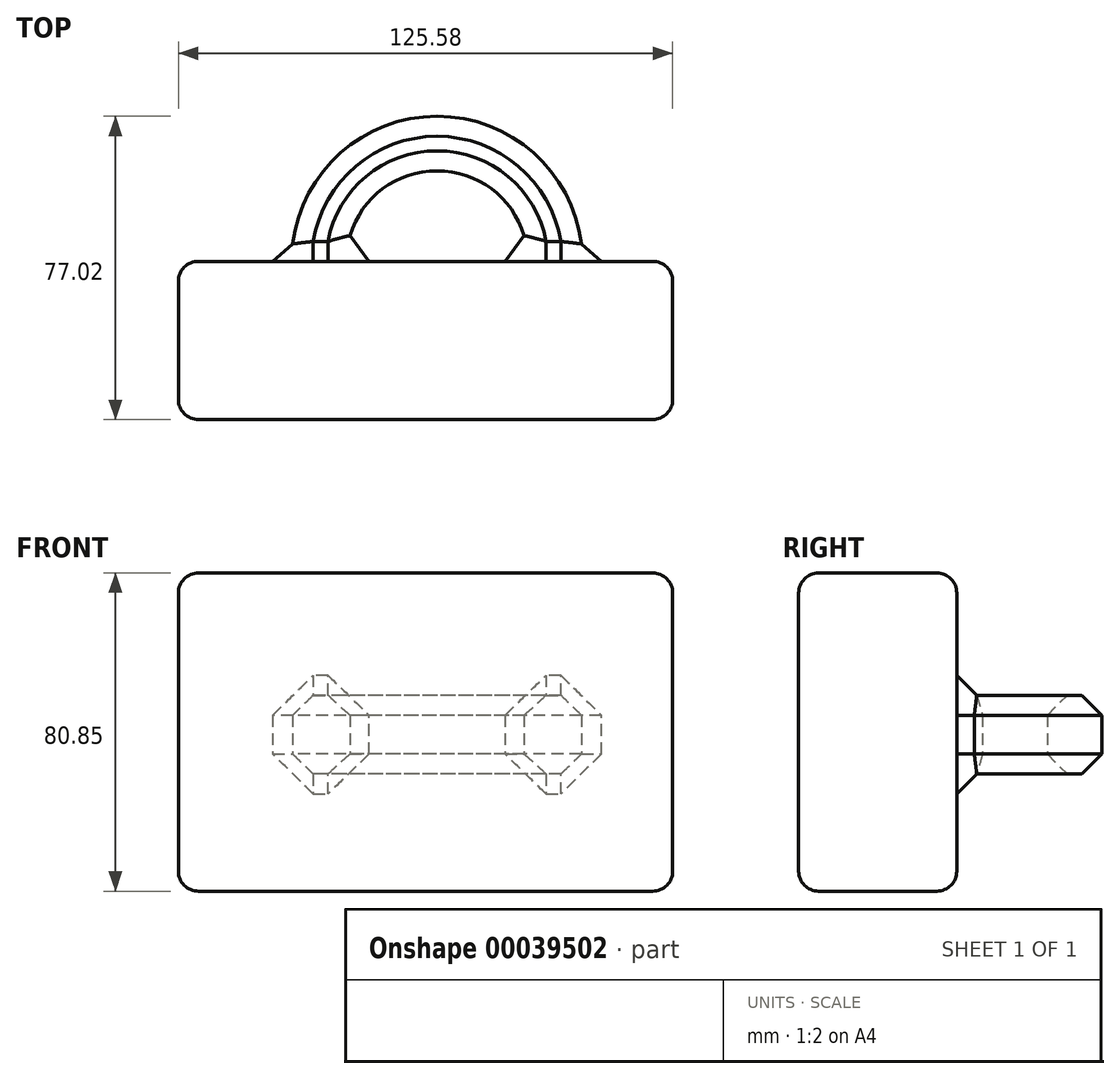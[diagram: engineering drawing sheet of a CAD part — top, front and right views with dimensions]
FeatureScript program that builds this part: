
annotation { "Feature Type Name" : "Feature", "Feature Type Description" : "" }
export const myFeature = defineFeature(function(context is Context, id is Id, definition is map)
    precondition{}
    {
        {
            var Q0;
            Q0=qCreatedBy(makeId("Top.planeOp"),FACE);
            var sketch = newSketch(context, id + "F0", { "sketchPlane" : qUnion([Q0])});
            skCircle(sketch, "E0", {"center": v(0.24, -0.12) * mm, "radius": 36.97 * mm});
            skCircle(sketch, "E1", {"center": v(0.24, -0.12) * mm, "radius": 23.11 * mm});
            skSolve(sketch);
        }
        {
            var Q0;
            Q0=makeQuery(id+"F0.imprint","IMPRINT",FACE,{"disambiguationData":[TD([[makeQuery(id+"F0.imprint","IMPRINT",EDGE,{"derivedFrom":sQuery(id+"F0.wireOp",EDGE,"E0")}),1.0]])]});
            extrude(context, id + "F1", {"entities" : qUnion([Q0]), "depth" : 20 * mm});
        }
        {
            var Q0;
            Q0=qCreatedBy(makeId("Front.planeOp"),FACE);
            var sketch = newSketch(context, id + "F2", { "sketchPlane" : qUnion([Q0])});
            skLineSegment(sketch, "E2.bottom", {"start": v(60.11, 51.07) * mm, "end": v(-65.47, 51.07) * mm});
            skLineSegment(sketch, "E2.top", {"start": v(60.11, -29.78) * mm, "end": v(-65.47, -29.78) * mm});
            skLineSegment(sketch, "E2.left", {"start": v(60.11, 51.07) * mm, "end": v(60.11, -29.78) * mm});
            skLineSegment(sketch, "E2.right", {"start": v(-65.47, 51.07) * mm, "end": v(-65.47, -29.78) * mm});
            skSolve(sketch);
        }
        {
            var Q0;
            Q0=makeQuery(id+"F2.imprint","IMPRINT",FACE,{"disambiguationData":[TD([[makeQuery(id+"F2.imprint","IMPRINT",EDGE,{"derivedFrom":sQuery(id+"F2.wireOp",EDGE,"E2.bottom")}),1.0]])]});
            extrude(context, id + "F3", {"entities" : qUnion([Q0]), "operationType" : NewBodyOperationType.ADD, "depth" : 40.17 * mm});
        }
        {
            var Q0;
            Q0=makeQuery(id+"F3.opExtrude","SWEPT_FACE",FACE,{"disambiguationData":[OSD([sQuery(id+"F2.wireOp",EDGE,"E2.bottom")])]});
            var Q1;
            Q1=makeQuery(id+"F3.opExtrude","CAP_FACE",FACE,{"disambiguationData":[OSD([sQuery(id+"F2.wireOp",EDGE,"E2.bottom"),sQuery(id+"F2.wireOp",EDGE,"E2.top"),sQuery(id+"F2.wireOp",EDGE,"E2.left"),sQuery(id+"F2.wireOp",EDGE,"E2.right")])],"isStart":false});
            var Q2;
            Q2=makeQuery(id+"F3.opExtrude","SWEPT_FACE",FACE,{"disambiguationData":[OSD([sQuery(id+"F2.wireOp",EDGE,"E2.left")])]});
            var Q3;
            Q3=makeQuery(id+"F3.opExtrude","SWEPT_FACE",FACE,{"disambiguationData":[OSD([sQuery(id+"F2.wireOp",EDGE,"E2.top")])]});
            var Q4;
            Q4=makeQuery(id+"F3.opExtrude","SWEPT_FACE",FACE,{"disambiguationData":[OSD([sQuery(id+"F2.wireOp",EDGE,"E2.right")])]});
            fillet(context, id + "F4", {"entities" : qUnion([Q0, Q1, Q2, Q3, Q4]), "radius" : 5.08 * mm, "tangentPropagation" : true, "allowEdgeOverflow" : false});
        }
        {
            var Q0;
            Q0=makeQuery(id+"F1.opExtrude","CAP_EDGE",EDGE,{"disambiguationData":[OSD([sQuery(id+"F0.wireOp",EDGE,"E1")])],"isStart":true});
            var Q1;
            Q1=makeQuery(id+"F1.opExtrude","CAP_FACE",FACE,{"disambiguationData":[OSD([sQuery(id+"F0.wireOp",EDGE,"E0"),sQuery(id+"F0.wireOp",EDGE,"E1")])],"isStart":true});
            var Q2;
            Q2=makeQuery(id+"F1.opExtrude","CAP_FACE",FACE,{"disambiguationData":[OSD([sQuery(id+"F0.wireOp",EDGE,"E0"),sQuery(id+"F0.wireOp",EDGE,"E1")])],"isStart":false});
            chamfer(context, id + "F5", {"entities" : qUnion([Q0, Q1, Q2]), "width" : 5.08 * mm, "tangentPropagation" : true});
        }
    });
